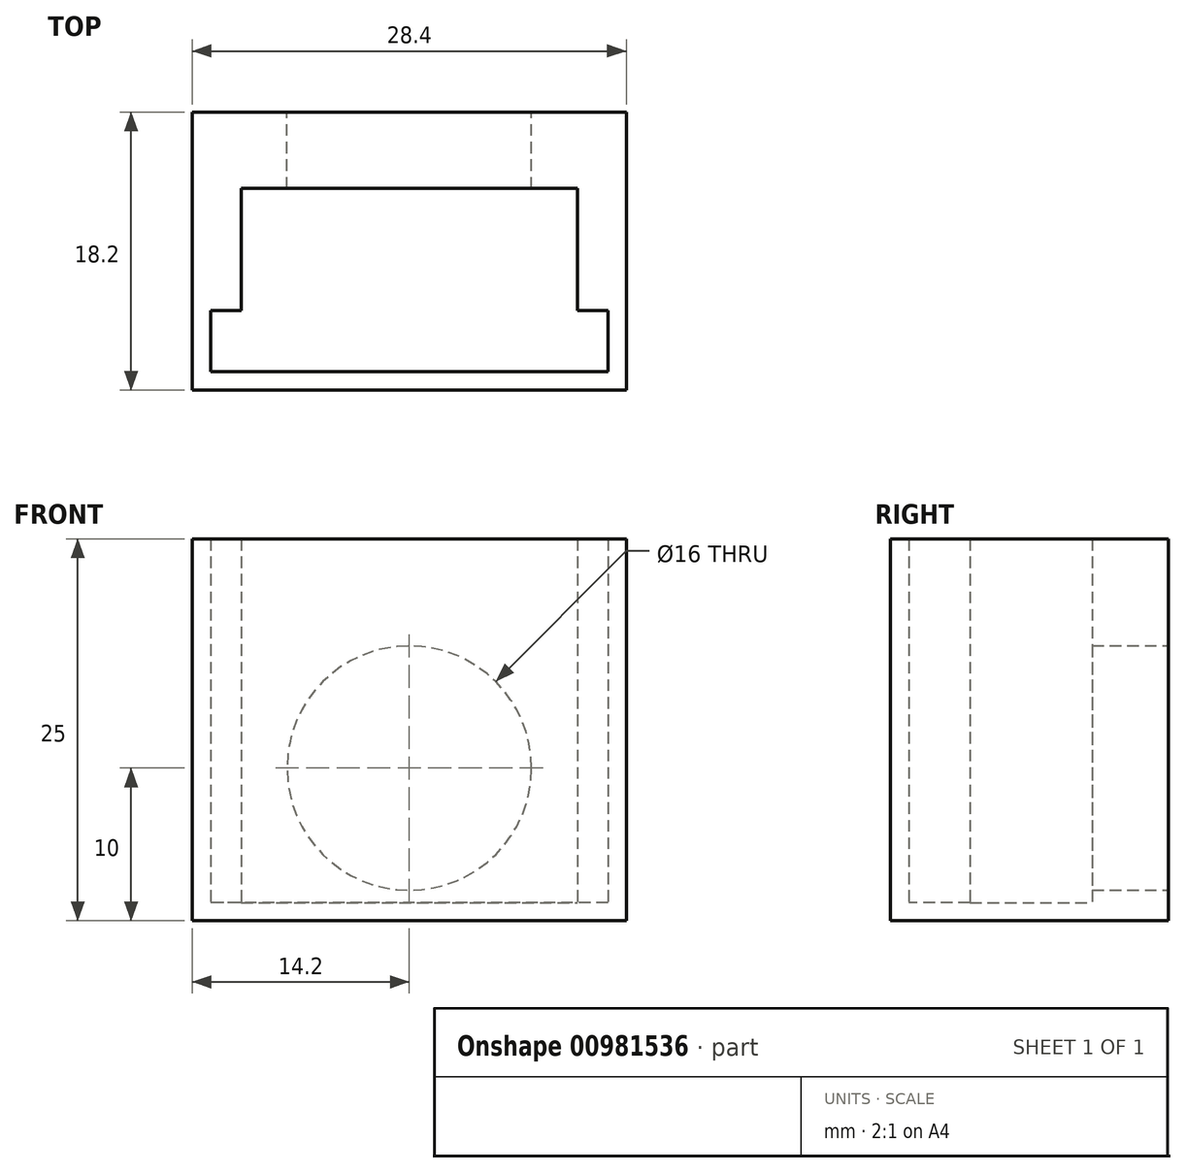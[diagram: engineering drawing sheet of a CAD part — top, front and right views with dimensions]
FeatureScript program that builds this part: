
annotation { "Feature Type Name" : "Feature", "Feature Type Description" : "" }
export const myFeature = defineFeature(function(context is Context, id is Id, definition is map)
    precondition{}
    {
        {
            var Q0;
            Q0=qCreatedBy(makeId("Top.planeOp"),FACE);
            var sketch = newSketch(context, id + "F0", { "sketchPlane" : qUnion([Q0])});
            skLineSegment(sketch, "E0.bottom", {"start": v(13, 2) * mm, "end": v(-13, 2) * mm});
            skLineSegment(sketch, "E0.top", {"start": v(13, -2) * mm, "end": v(-13, -2) * mm});
            skLineSegment(sketch, "E0.left", {"start": v(13, 2) * mm, "end": v(13, -2) * mm});
            skLineSegment(sketch, "E0.right", {"start": v(-13, 2) * mm, "end": v(-13, -2) * mm});
            skPoint(sketch, "E0.middle", {"position": v(0, 0) * mm});
            skLineSegment(sketch, "E1", {"start": v(-11, 2) * mm, "end": v(-11, 10) * mm});
            skLineSegment(sketch, "E2", {"start": v(-11, 10) * mm, "end": v(11, 10) * mm});
            skLineSegment(sketch, "E3", {"start": v(11, 10) * mm, "end": v(11, 2) * mm});
            skPoint(sketch, "E4", {"position": v(0, 10) * mm});
            skLineSegment(sketch, "E5.bottom", {"start": v(-14.2, 15) * mm, "end": v(14.2, 15) * mm});
            skLineSegment(sketch, "E5.top", {"start": v(-14.2, -3.2) * mm, "end": v(14.2, -3.2) * mm});
            skLineSegment(sketch, "E5.left", {"start": v(-14.2, 15) * mm, "end": v(-14.2, -3.2) * mm});
            skLineSegment(sketch, "E5.right", {"start": v(14.2, 15) * mm, "end": v(14.2, -3.2) * mm});
            skSolve(sketch);
        }
        {
            var Q0;
            Q0 = qSketchRegion(id + "F0", true);
            extrude(context, id + "F1", {"entities" : qUnion([Q0]), "depth" : 25 * mm, "offsetDistance" : 25 * mm});
        }
        {
            var Q0;
            {var subQ0=sQuery(id+"F0.wireOp",EDGE,"E1");Q0=makeQuery(id+"F0.imprint","IMPRINT",FACE,{"disambiguationData":[TD([[makeQuery(id+"F0.imprint","IMPRINT",EDGE,{"derivedFrom":subQ0}),-1.0]])]});}
            var Q1;
            Q1=makeQuery(id+"F0.imprint","IMPRINT",FACE,{"disambiguationData":[TD([[makeQuery(id+"F0.imprint","IMPRINT",EDGE,{"derivedFrom":sQuery(id+"F0.wireOp",EDGE,"E0.top")}),-1.0]])]});
            extrude(context, id + "F2", {"entities" : qUnion([Q0, Q1]), "operationType" : NewBodyOperationType.ADD, "depth" : 1.2 * mm, "offsetDistance" : 25 * mm});
        }
        {
            var Q0;
            Q0=makeQuery(id+"F1.opExtrude","SWEPT_FACE",FACE,{"disambiguationData":[OSD([sQuery(id+"F0.wireOp",EDGE,"E5.bottom")])]});
            var sketch = newSketch(context, id + "F3", { "sketchPlane" : qUnion([Q0])});
            skCircle(sketch, "E6", {"center": v(0, 10) * mm, "radius": 8 * mm});
            skSolve(sketch);
        }
        {
            var Q0;
            {var subQ0=sQuery(id+"F3.wireOp",EDGE,"E6");var subQ1=makeQuery(id+"F1.opExtrude","CAP_EDGE",EDGE,{"disambiguationData":[OSD([sQuery(id+"F0.wireOp",EDGE,"E5.bottom")])],"isStart":true});var subQ2=makeQuery(id+"F3.imprint","INTERSECT",VERTEX,{"disambiguationData":[OD(0.0)],"derivedFrom":[subQ1,subQ0]});Q0=makeQuery(id+"F3.imprint","IMPRINT",FACE,{"disambiguationData":[TD([[makeQuery(id+"F3.imprint","IMPRINT",EDGE,{"disambiguationData":[TD([[subQ2,-1.0]])],"derivedFrom":subQ0}),1.0]])]});}
            extrude(context, id + "F4", {"entities" : qUnion([Q0]), "operationType" : NewBodyOperationType.REMOVE, "oppositeDirection" : true, "depth" : 5 * mm, "offsetDistance" : 25 * mm});
        }
    });
